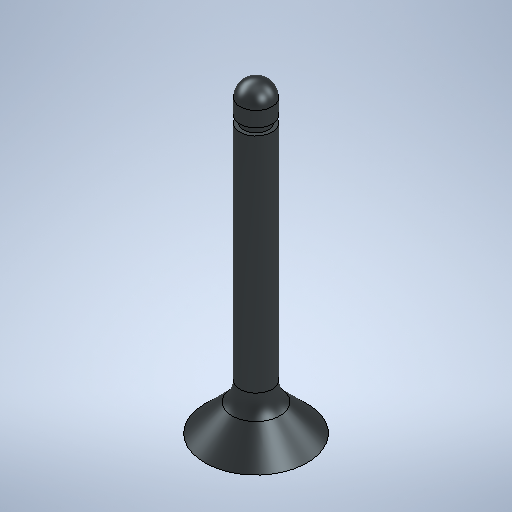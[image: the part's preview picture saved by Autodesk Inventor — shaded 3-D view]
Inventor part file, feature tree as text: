
AUTODESK INVENTOR PART (.ipt)
format: ipt  version: 2025 (Build 290162010, 162A)  size: 283,648 bytes
history: native  units: mm
features: revolve x1, fillet x1, sketch x1
ambient origin geometry x8: Origin, YZ Plane, XZ Plane, XY Plane, X Axis, Y Axis, Z Axis, Center Point
bodies: Solid1 (feature_tree)
feature tree (3):
  revolve  "Revolution1"  [1 undecoded]
  fillet  "Fillet1"  Radius=3.0mm
  sketch  "Sketch1"  dims[d4=45.0deg d5=9.5mm d6=3.0mm d7=0.65mm d8=2.3mm d9=2.9mm d10=28.5mm d11=90.0deg d12=2.5mm]
note: 1 required parameter value undecoded (feature->parameter linkage not recoverable at this tier; creation-order binding heuristic only, values carry confidence <= 0.55)
